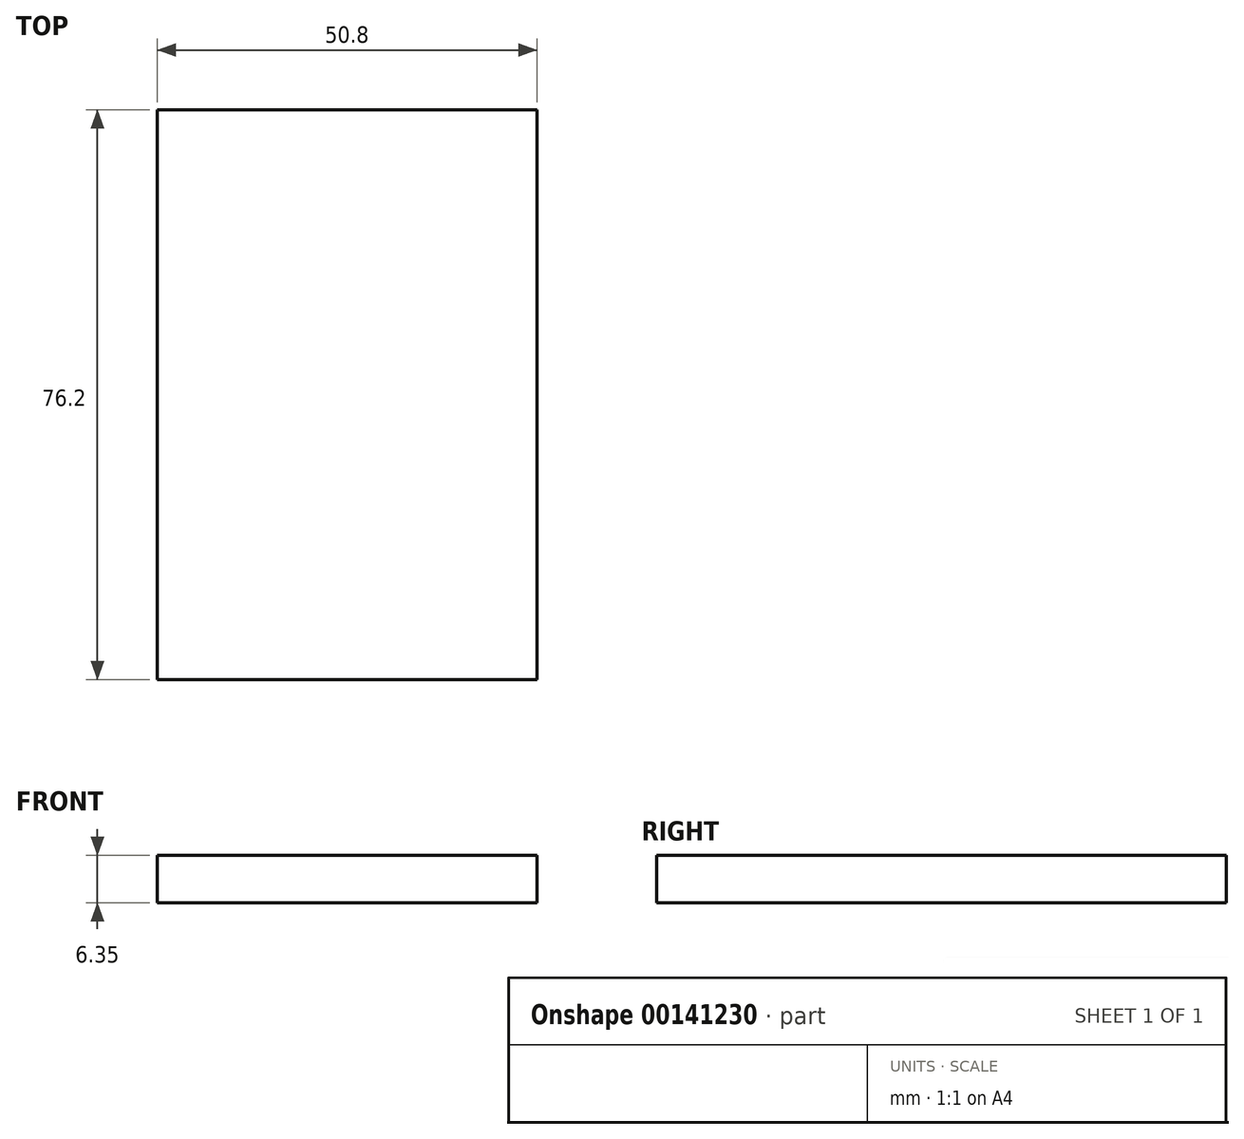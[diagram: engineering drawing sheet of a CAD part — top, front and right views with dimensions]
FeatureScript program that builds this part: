
annotation { "Feature Type Name" : "Feature", "Feature Type Description" : "" }
export const myFeature = defineFeature(function(context is Context, id is Id, definition is map)
    precondition{}
    {
        {
            var Q0;
            Q0=qCreatedBy(makeId("Top.planeOp"),FACE);
            var sketch = newSketch(context, id + "F0", { "sketchPlane" : qUnion([Q0])});
            skLineSegment(sketch, "E0", {"start": v(-59.74, -35.28) * mm, "end": v(-8.94, -35.28) * mm});
            skLineSegment(sketch, "E1", {"start": v(-8.94, -35.28) * mm, "end": v(-8.94, 40.92) * mm});
            skLineSegment(sketch, "E2", {"start": v(-8.94, 40.92) * mm, "end": v(-59.74, 40.92) * mm});
            skLineSegment(sketch, "E3", {"start": v(-59.74, 40.92) * mm, "end": v(-59.74, -35.28) * mm});
            skSolve(sketch);
        }
        {
            var Q0;
            Q0 = qSketchRegion(id + "F0", true);
            extrude(context, id + "F1", {"entities" : qUnion([Q0]), "depth" : 6.35 * mm});
        }
    });
